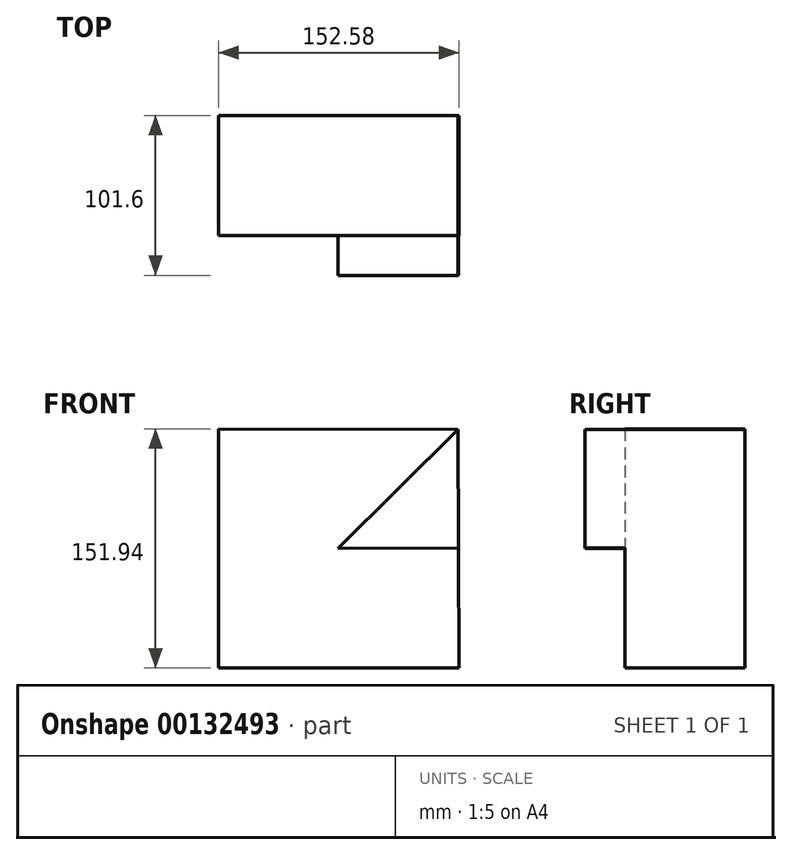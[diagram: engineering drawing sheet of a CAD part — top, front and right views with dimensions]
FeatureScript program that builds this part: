
annotation { "Feature Type Name" : "Feature", "Feature Type Description" : "" }
export const myFeature = defineFeature(function(context is Context, id is Id, definition is map)
    precondition{}
    {
        {
            var Q0;
            Q0=qCreatedBy(makeId("Front.planeOp"),FACE);
            var sketch = newSketch(context, id + "F0", { "sketchPlane" : qUnion([Q0])});
            skLineSegment(sketch, "E0", {"start": v(0, 0) * mm, "end": v(76.61, 0) * mm});
            skLineSegment(sketch, "E1", {"start": v(76.61, 0) * mm, "end": v(-76.3, 0) * mm});
            skLineSegment(sketch, "E2", {"start": v(75.97, 75.5) * mm, "end": v(76.61, -76.13) * mm});
            skLineSegment(sketch, "E3", {"start": v(76.61, -76.13) * mm, "end": v(-75.97, -76.13) * mm});
            skLineSegment(sketch, "E4", {"start": v(-75.97, -76.13) * mm, "end": v(-75.97, 75.81) * mm});
            skLineSegment(sketch, "E5", {"start": v(-75.97, 75.81) * mm, "end": v(75.97, 75.5) * mm});
            skSolve(sketch);
        }
        {
            var Q0;
            {var subQ0=sQuery(id+"F0.wireOp",EDGE,"E5");Q0=makeQuery(id+"F0.imprint","IMPRINT",FACE,{"disambiguationData":[TD([[makeQuery(id+"F0.imprint","IMPRINT",EDGE,{"derivedFrom":subQ0}),-1.0]])]});}
            var Q1;
            {var subQ0=sQuery(id+"F0.wireOp",EDGE,"E3");Q1=makeQuery(id+"F0.imprint","IMPRINT",FACE,{"disambiguationData":[TD([[makeQuery(id+"F0.imprint","IMPRINT",EDGE,{"derivedFrom":subQ0}),-1.0]])]});}
            extrude(context, id + "F1", {"entities" : qUnion([Q0, Q1]), "depth" : 76.2 * mm});
        }
        {
            var Q0;
            Q0=makeQuery(id+"F1.opExtrude","CAP_FACE",FACE,{"disambiguationData":[OSD([sQuery(id+"F0.wireOp",EDGE,"E2"),sQuery(id+"F0.wireOp",EDGE,"E3"),sQuery(id+"F0.wireOp",EDGE,"E4"),sQuery(id+"F0.wireOp",EDGE,"E5")])],"isStart":false});
            var sketch = newSketch(context, id + "F2", { "sketchPlane" : qUnion([Q0])});
            skLineSegment(sketch, "E6", {"start": v(0, 0) * mm, "end": v(76.3, 0.32) * mm});
            skLineSegment(sketch, "E7", {"start": v(76.3, 0.32) * mm, "end": v(75.97, 75.5) * mm});
            skLineSegment(sketch, "E8", {"start": v(75.97, 75.5) * mm, "end": v(0, 0) * mm});
            skSolve(sketch);
        }
        {
            var Q0;
            Q0=makeQuery(id+"F2.imprint","IMPRINT",FACE,{"disambiguationData":[TD([[makeQuery(id+"F2.imprint","IMPRINT",EDGE,{"derivedFrom":sQuery(id+"F2.wireOp",EDGE,"E6")}),1.0]])]});
            extrude(context, id + "F3", {"entities" : qUnion([Q0]), "operationType" : NewBodyOperationType.ADD, "depth" : 25.4 * mm});
        }
    });
